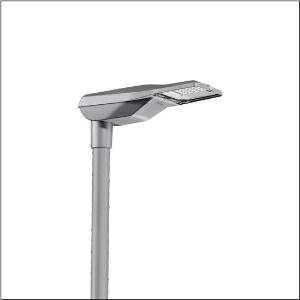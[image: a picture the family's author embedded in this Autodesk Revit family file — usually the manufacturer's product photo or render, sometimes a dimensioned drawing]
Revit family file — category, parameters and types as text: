
# Revit family: streetlight_sl_21_iq_micro___st1_0a_5xe1d31d08db_2abd
name_source: partatom
category: Lighting Fixtures
units: mm (PartAtom-declared; Revit-internal decimal feet)

## family parameters
Cut with Voids When Loaded = No
Host = Face
Light Source = No
Part Type = Normal
Room Calculation Point = No
Round Connector Dimension = Use Diameter
Shared = No

## types (1)
- --- (1 x LED, 4810 lm, 36.4 W, 3000K)
    Apparent Load = 36 VA
    CIE Flux Codes = 37 72 97 100 100
    Color Rendering = 70
    Color Temperature = 3000K
    Default Elevation = 1800 mm
    Description = Streetlight SL 21 iQ micro, mast luminaire, primary light control with lens, of PMMA, primary optical cover: cover, of toughened safety glass, transparent, light distribution: ST1.0a, light emission: direct distribution, primary light characteristic: asymmetric, installation type: post-top, side-entry, LED, High Power LED, rated luminous flux: 4.810lm, luminous efficacy: 132lm/W, light colour: 730, colour temperature: 3000K, control: Auto-Match, Temp-Guard, Lumen-Switch, Night-Set, Smart-Wire, Light-Fading, Desk-Remote (wireless, voltage-free reading and setting of iQ features in the workshop via application-optimized NFC function/RFID function), optimised constant luminous flux control (CLO 2.0), presetting dimming linear, mains connection: 220..240V, AC, 50/60Hz, start of lifetime: 36W, end of service life: 38W, reduction: 16W, luminaire housing, of diecast aluminium, powder-coated, Siteco® metallic grey (DB 702S), corrosivity category C5 mid according to DIN EN ISO 12944, please order mast flange separately, inclination adjustable: 0°, 5°, 10°, 15°, sealing non-destructively replaceable, multi-level sealing system, length: 528mm, width: 235mm, height: 110mm, mast flange for spigot size: 42mm (side-entry): 5XC10008XM4, 60/48mm (side-entry/post-top): 5XC10108XM2, 76/60mm (side-entry/post-top): 5XC10108XM1, protection rating (complete): IP66, insulation class (complete): insulation class II (safety insulation), certification: CE, ENEC, ENEC+, VDE, impact resistance: IK09, permissible operating ambient temperature for outdoor applications: -40..+50°C, standard-compliant lighting for roads and squares, packaging unit: 1 piece

Light Distribution: ST1.0a
    Height = 110 mm
    Lamp = 1 x LED
    Lamp Light Flux = 4810 lm
    Lamp Power = 36.4 W
    Lamp count = 1
    Length = 528 mm
    Luminous efficacy = 132 lm/W
    Manufacturer = Siteco
    ModVariant = No
    Model = 5XE1D31D08DB
    Number of Poles = 1
    OnlyDefault = Yes
    Power Factor = 1
    Product Name = Streetlight SL 21 iQ micro | ST1.0a
    Product group = mast luminaire | pylon top
    ProductGroupID = 6100
    Protection Class = Protection class II
    Protection Degree = IP 66
    RLX_Detail_Level = 1
    RLX_Emergency_Light_Flux = 0 lm
    RLX_Emergency_Type = 0
    RLX_Emergency_Type_DB = No
    RlxData = <blob elided: 99013 chars, md5=296e876e>
    Socket = socket
    Standby Power = 0 W
    System Light Flux = 4810 lm
    System Power = 36 W
    Type Comments = factory setting: luminous flux: 100 % | dim-lin: 254 | 715 mA
    Type Image = l_1006881.jpg
    URL = http://relux.com
    VarID = @adj_088329
    Voltage = 0 V
    Weight = 0.00 kg
    Width = 235 mm

## geometry (parser evidence)
native form markers: Blend x4, Sweep x12
no freeform markers — native parametric forms only
